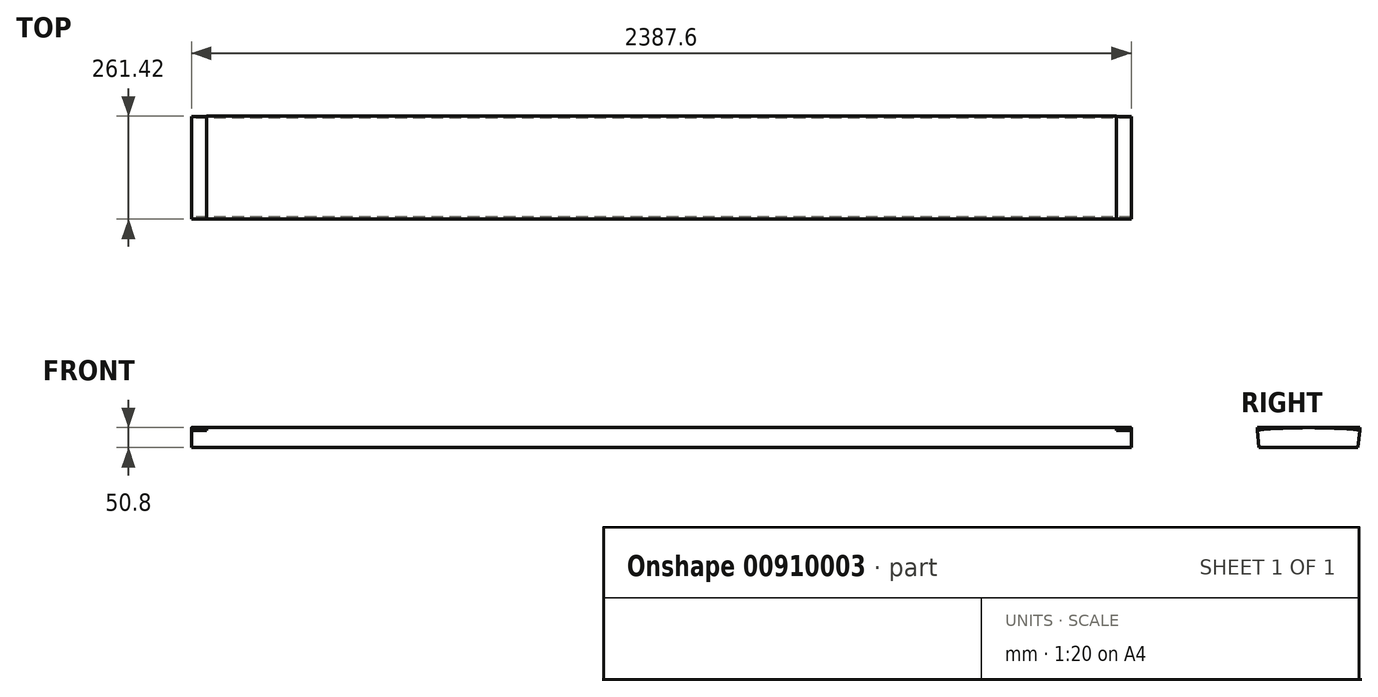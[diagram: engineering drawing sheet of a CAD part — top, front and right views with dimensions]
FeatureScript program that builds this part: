
annotation { "Feature Type Name" : "Feature", "Feature Type Description" : "" }
export const myFeature = defineFeature(function(context is Context, id is Id, definition is map)
    precondition{}
    {
        {
            var Q0;
            Q0=qCreatedBy(makeId("Right.planeOp"),FACE);
            var sketch = newSketch(context, id + "F0", { "sketchPlane" : qUnion([Q0])});
            skCircle(sketch, "E0", {"center": v(0, 0) * mm, "radius": 1327.15 * mm});
            skLineSegment(sketch, "E1", {"start": v(-130.71, 1327.15) * mm, "end": v(130.71, 1327.15) * mm});
            skLineSegment(sketch, "E2", {"start": v(-130.71, 1327.15) * mm, "end": v(-125.7, 1276.35) * mm});
            skLineSegment(sketch, "E3", {"start": v(130.71, 1327.15) * mm, "end": v(125.7, 1276.35) * mm});
            skLineSegment(sketch, "E4", {"start": v(0, 0) * mm, "end": v(0, 1327.15) * mm, "construction": true});
            skLineSegment(sketch, "E5", {"start": v(-130.71, 1327.15) * mm, "end": v(-130.71, 1276.35) * mm});
            skLineSegment(sketch, "E6", {"start": v(-130.71, 1276.35) * mm, "end": v(130.71, 1276.35) * mm});
            skLineSegment(sketch, "E7", {"start": v(130.71, 1276.35) * mm, "end": v(130.71, 1327.15) * mm});
            skSolve(sketch);
        }
        {
            var Q0;
            {var subQ3=sQuery(id+"F0.wireOp",EDGE,"E0");var subQ8=makeQuery(id+"F0.imprint","INTERSECT",VERTEX,{"derivedFrom":[subQ3,sQuery(id+"F0.wireOp",EDGE,"E1")]});Q0=makeQuery(id+"F0.imprint","IMPRINT",FACE,{"disambiguationData":[TD([[makeQuery(id+"F0.imprint","IMPRINT",EDGE,{"disambiguationData":[TD([[subQ8,1.0]])],"derivedFrom":subQ3}),1.0]])]});}
            extrude(context, id + "F1", {"entities" : qUnion([Q0]), "depth" : 2387.6 * mm, "offsetDistance" : 25 * mm, "symmetric" : true});
        }
        {
            var Q0;
            {var subQ0=sQuery(id+"F0.wireOp",EDGE,"E1");var subQ1=sQuery(id+"F0.wireOp",EDGE,"E0");var subQ2=makeQuery(id+"F0.imprint","INTERSECT",VERTEX,{"derivedFrom":[subQ1,subQ0]});Q0=makeQuery(id+"F0.imprint","IMPRINT",FACE,{"disambiguationData":[TD([[makeQuery(id+"F0.imprint","IMPRINT",EDGE,{"disambiguationData":[TD([[subQ2,-1.0]])],"derivedFrom":subQ1}),-1.0]])]});}
            var Q1;
            {var subQ0=sQuery(id+"F0.wireOp",EDGE,"E1");var subQ1=sQuery(id+"F0.wireOp",EDGE,"E0");var subQ2=makeQuery(id+"F0.imprint","INTERSECT",VERTEX,{"derivedFrom":[subQ1,subQ0]});Q1=makeQuery(id+"F0.imprint","IMPRINT",FACE,{"disambiguationData":[TD([[makeQuery(id+"F0.imprint","IMPRINT",EDGE,{"disambiguationData":[TD([[subQ2,1.0]])],"derivedFrom":subQ1}),-1.0]])]});}
            extrude(context, id + "F2", {"entities" : qUnion([Q0, Q1]), "operationType" : NewBodyOperationType.ADD, "depth" : 2311.4 * mm, "offsetDistance" : 25 * mm, "symmetric" : true});
        }
    });
